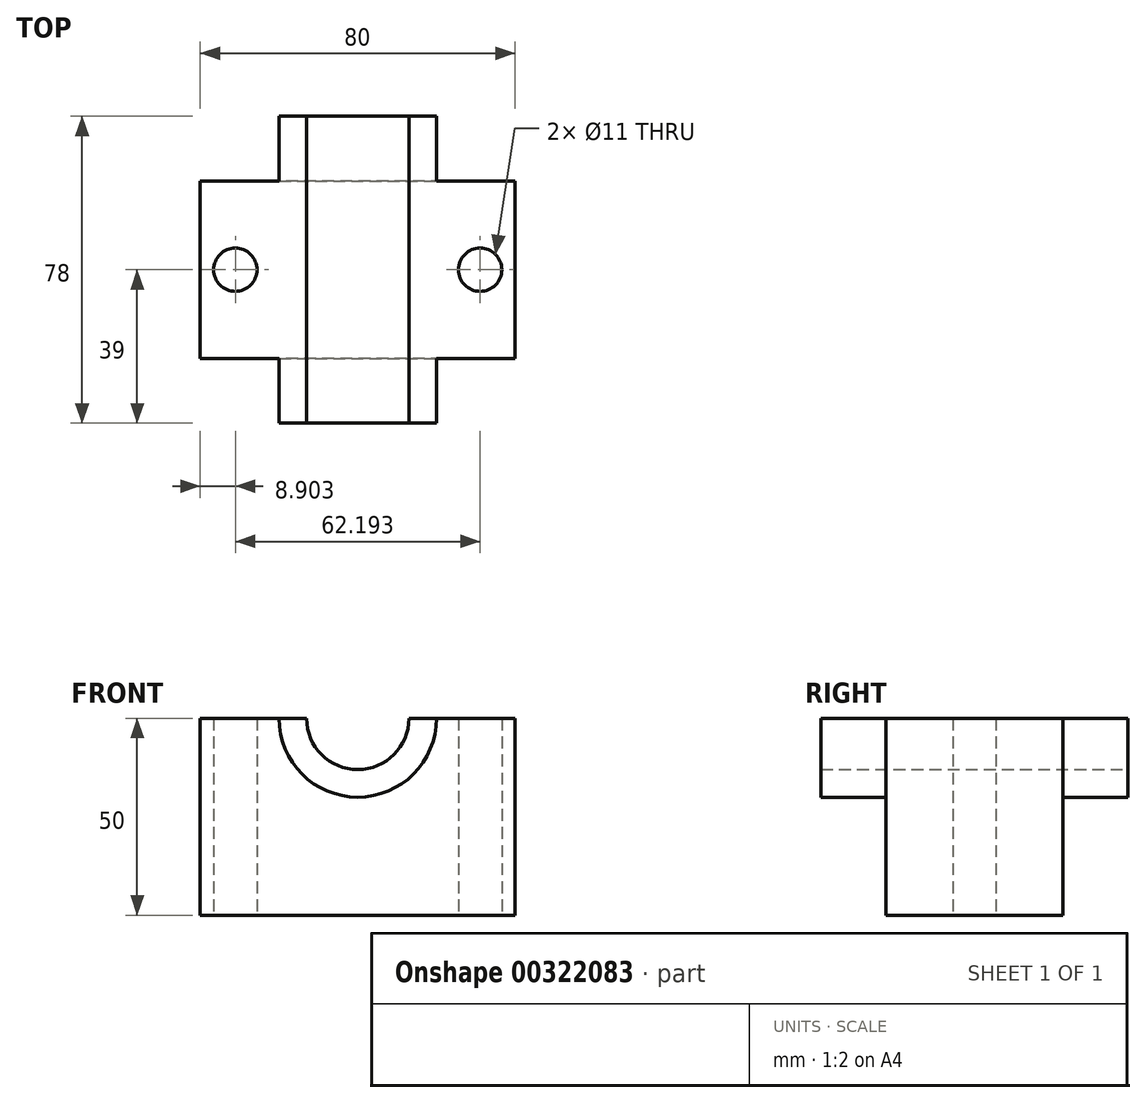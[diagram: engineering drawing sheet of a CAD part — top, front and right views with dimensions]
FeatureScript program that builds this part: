
annotation { "Feature Type Name" : "Feature", "Feature Type Description" : "" }
export const myFeature = defineFeature(function(context is Context, id is Id, definition is map)
    precondition{}
    {
        {
            var Q0;
            Q0=qCreatedBy(makeId("Top.planeOp"),FACE);
            var sketch = newSketch(context, id + "F0", { "sketchPlane" : qUnion([Q0])});
            skLineSegment(sketch, "E0.bottom", {"start": v(40, -22.5) * mm, "end": v(-40, -22.5) * mm});
            skLineSegment(sketch, "E0.top", {"start": v(40, 22.5) * mm, "end": v(-40, 22.5) * mm});
            skLineSegment(sketch, "E0.left", {"start": v(40, -22.5) * mm, "end": v(40, 22.5) * mm});
            skLineSegment(sketch, "E0.right", {"start": v(-40, -22.5) * mm, "end": v(-40, 22.5) * mm});
            skPoint(sketch, "E0.middle", {"position": v(0, 0) * mm});
            skCircle(sketch, "E1", {"center": v(31.1, 0) * mm, "radius": 5.5 * mm});
            skCircle(sketch, "E2.MirrorC", {"center": v(-31.1, 0) * mm, "radius": 5.5 * mm});
            skSolve(sketch);
        }
        {
            var Q0;
            Q0=makeQuery(id+"F0.imprint","IMPRINT",FACE,{"disambiguationData":[TD([[makeQuery(id+"F0.imprint","IMPRINT",EDGE,{"derivedFrom":sQuery(id+"F0.wireOp",EDGE,"E0.bottom")}),-1.0]])]});
            extrude(context, id + "F1", {"entities" : qUnion([Q0]), "depth" : 50 * mm});
        }
        {
            var Q0;
            Q0=qCreatedBy(makeId("Front.planeOp"),FACE);
            var sketch = newSketch(context, id + "F2", { "sketchPlane" : qUnion([Q0])});
            skLineSegment(sketch, "E3.0", {"start": v(20, 50) * mm, "end": v(13, 50) * mm});
            skArc(sketch, "E4", {"start": v(-20, 50) * mm, "mid": v(0, 30) * mm, "end": v(20, 50) * mm});
            skArc(sketch, "E5", {"start": v(-13, 50) * mm, "mid": v(0, 37) * mm, "end": v(13, 50) * mm});
            skPoint(sketch, "E6.orphan", {"position": v(-40, 50) * mm});
            skPoint(sketch, "E7.orphan", {"position": v(40, 50) * mm});
            skLineSegment(sketch, "E8.trimOffspring", {"start": v(-13, 50) * mm, "end": v(-20, 50) * mm});
            skSolve(sketch);
        }
        {
            var Q0;
            Q0 = qSketchRegion(id + "F2", true);
            extrude(context, id + "F3", {"entities" : qUnion([Q0]), "operationType" : NewBodyOperationType.ADD, "endBound" : BoundingType.SYMMETRIC, "depth" : 78 * mm});
        }
        {
            var Q0;
            {var subQ0=sQuery(id+"F0.wireOp",EDGE,"E0.bottom");Q0=makeQuery(id+"F3.boolean.opBoolean","SPLIT",FACE,{"disambiguationData":[TD([makeQuery(id+"F3.opExtrude","SWEPT_FACE",FACE,{"disambiguationData":[OSD([sQuery(id+"F2.wireOp",EDGE,"E5")])]})])],"derivedFrom":makeQuery(id+"F1.opExtrude","SWEPT_FACE",FACE,{"disambiguationData":[OSD([subQ0])]})});}
            var Q1;
            {var subQ0=sQuery(id+"F0.wireOp",EDGE,"E0.top");Q1=makeQuery(id+"F3.boolean.opBoolean","SPLIT",FACE,{"disambiguationData":[TD([makeQuery(id+"F3.opExtrude","SWEPT_FACE",FACE,{"disambiguationData":[OSD([sQuery(id+"F2.wireOp",EDGE,"E5")])]})])],"derivedFrom":makeQuery(id+"F1.opExtrude","SWEPT_FACE",FACE,{"disambiguationData":[OSD([subQ0])]})});}
            extrude(context, id + "F4", {"entities" : qUnion([Q0]), "operationType" : NewBodyOperationType.REMOVE, "endBound" : BoundingType.UP_TO_SURFACE, "oppositeDirection" : true, "endBoundEntityFace" : qUnion([Q1]), "depth" : 25 * mm});
        }
    });
